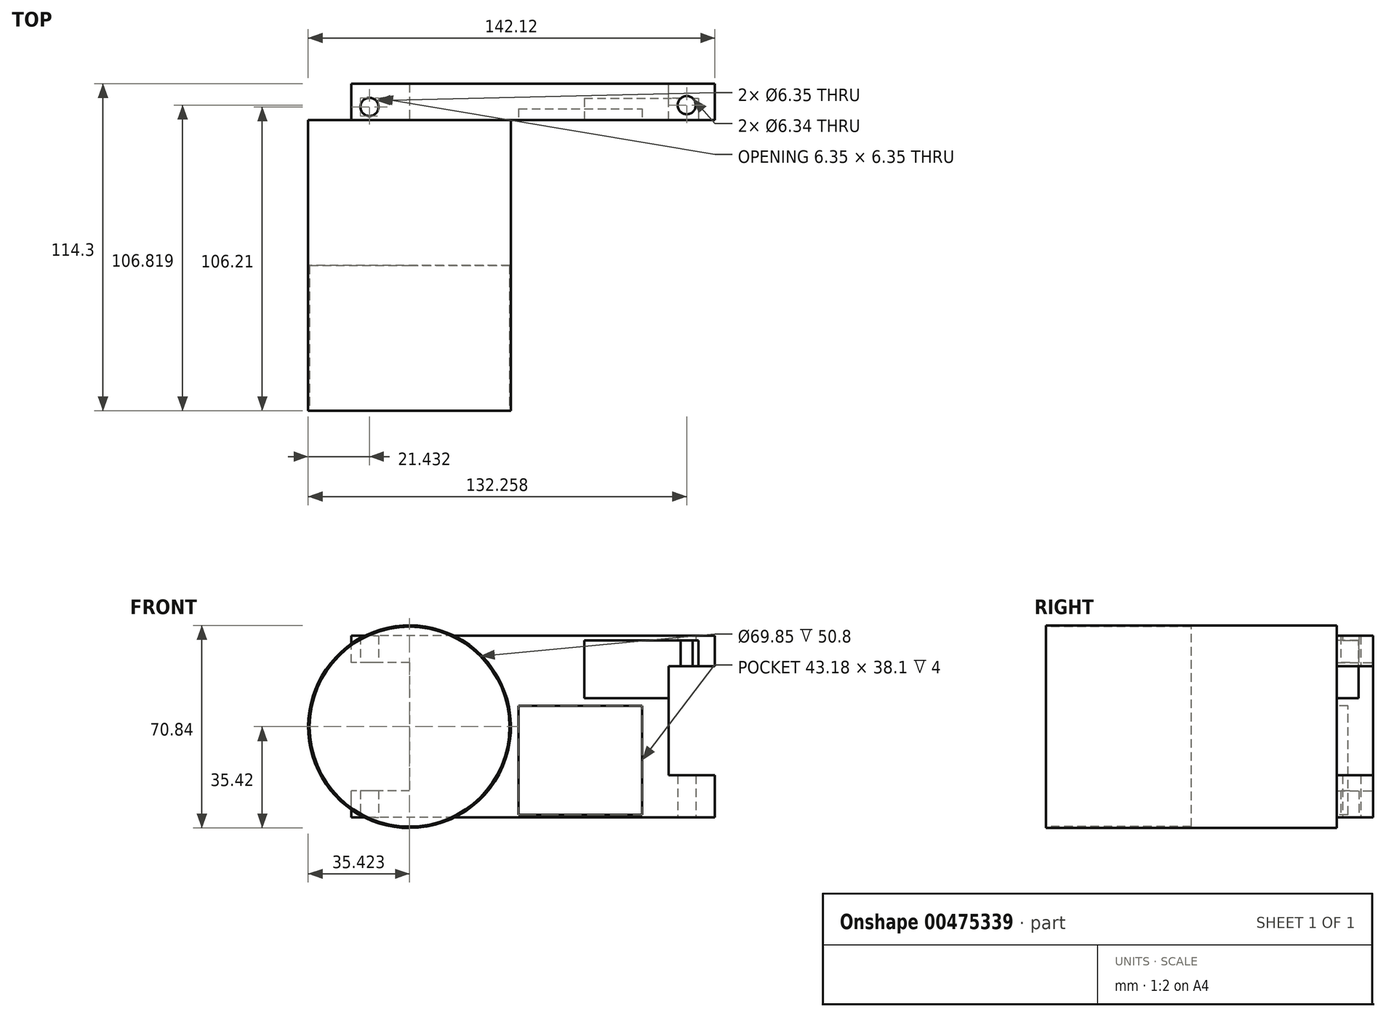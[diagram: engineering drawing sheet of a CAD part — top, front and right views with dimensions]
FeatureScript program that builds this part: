
annotation { "Feature Type Name" : "Feature", "Feature Type Description" : "" }
export const myFeature = defineFeature(function(context is Context, id is Id, definition is map)
    precondition{}
    {
        {
            var Q0;
            Q0=qCreatedBy(makeId("Front.planeOp"),FACE);
            var sketch = newSketch(context, id + "F0", { "sketchPlane" : qUnion([Q0])});
            skLineSegment(sketch, "E0.bottom", {"start": v(63.5, -31.75) * mm, "end": v(-63.5, -31.75) * mm});
            skLineSegment(sketch, "E0.top", {"start": v(63.5, 31.75) * mm, "end": v(-63.5, 31.75) * mm});
            skLineSegment(sketch, "E0.left", {"start": v(63.5, -31.75) * mm, "end": v(63.5, 31.75) * mm});
            skLineSegment(sketch, "E0.right", {"start": v(-63.5, -31.75) * mm, "end": v(-63.5, 31.75) * mm});
            skPoint(sketch, "E0.middle", {"position": v(0, 0) * mm});
            skSolve(sketch);
        }
        {
            var Q0;
            Q0 = qSketchRegion(id + "F0", true);
            extrude(context, id + "F1", {"entities" : qUnion([Q0]), "depth" : 12.7 * mm});
        }
        {
            var Q0;
            Q0=makeQuery(id+"F1.opExtrude","CAP_FACE",FACE,{"disambiguationData":[OSD([sQuery(id+"F0.wireOp",EDGE,"E0.bottom"),sQuery(id+"F0.wireOp",EDGE,"E0.top"),sQuery(id+"F0.wireOp",EDGE,"E0.left"),sQuery(id+"F0.wireOp",EDGE,"E0.right")])],"isStart":false});
            var sketch = newSketch(context, id + "F2", { "sketchPlane" : qUnion([Q0])});
            skLineSegment(sketch, "E1.bottom", {"start": v(-5.08, -30.75) * mm, "end": v(38.1, -30.75) * mm});
            skLineSegment(sketch, "E1.top", {"start": v(-5.08, 7.35) * mm, "end": v(38.1, 7.35) * mm});
            skLineSegment(sketch, "E1.left", {"start": v(-5.08, -30.75) * mm, "end": v(-5.08, 7.35) * mm});
            skLineSegment(sketch, "E1.right", {"start": v(38.1, -30.75) * mm, "end": v(38.1, 7.35) * mm});
            skPoint(sketch, "E1.middle", {"position": v(16.5, -11.7) * mm});
            skSolve(sketch);
        }
        {
            var Q0;
            Q0 = qSketchRegion(id + "F2", true);
            extrude(context, id + "F3", {"entities" : qUnion([Q0]), "operationType" : NewBodyOperationType.REMOVE, "oppositeDirection" : true, "depth" : 4 * mm});
        }
        {
            var Q0;
            Q0=makeQuery(id+"F1.opExtrude","CAP_FACE",FACE,{"disambiguationData":[OSD([sQuery(id+"F0.wireOp",EDGE,"E0.bottom"),sQuery(id+"F0.wireOp",EDGE,"E0.top"),sQuery(id+"F0.wireOp",EDGE,"E0.left"),sQuery(id+"F0.wireOp",EDGE,"E0.right")])],"isStart":false});
            var sketch = newSketch(context, id + "F4", { "sketchPlane" : qUnion([Q0])});
            skLineSegment(sketch, "E2.bottom", {"start": v(17.8, 9.95) * mm, "end": v(57.8, 9.95) * mm});
            skLineSegment(sketch, "E2.top", {"start": v(17.8, 30.1) * mm, "end": v(57.8, 30.1) * mm});
            skLineSegment(sketch, "E2.left", {"start": v(17.8, 9.95) * mm, "end": v(17.8, 30.1) * mm});
            skLineSegment(sketch, "E2.right", {"start": v(57.8, 9.95) * mm, "end": v(57.8, 30.1) * mm});
            skPoint(sketch, "E2.middle", {"position": v(37.8, 20.03) * mm});
            skSolve(sketch);
        }
        {
            var Q0;
            Q0 = qSketchRegion(id + "F4", true);
            extrude(context, id + "F5", {"entities" : qUnion([Q0]), "operationType" : NewBodyOperationType.REMOVE, "oppositeDirection" : true, "depth" : 7.62 * mm});
        }
        {
            var Q0;
            Q0=makeQuery(id+"F1.opExtrude","SWEPT_FACE",FACE,{"disambiguationData":[OSD([sQuery(id+"F0.wireOp",EDGE,"E0.bottom")])]});
            var sketch = newSketch(context, id + "F6", { "sketchPlane" : qUnion([Q0])});
            skCircle(sketch, "E3", {"center": v(53.64, 7.48) * mm, "radius": 3.17 * mm});
            skSolve(sketch);
        }
        {
            var Q0;
            Q0 = qSketchRegion(id + "F6", true);
            extrude(context, id + "F7", {"entities" : qUnion([Q0]), "operationType" : NewBodyOperationType.REMOVE, "endBound" : BoundingType.THROUGH_ALL, "oppositeDirection" : true, "depth" : 25.4 * mm});
        }
        {
            var Q0;
            Q0=makeQuery(id+"F1.opExtrude","SWEPT_FACE",FACE,{"disambiguationData":[OSD([sQuery(id+"F0.wireOp",EDGE,"E0.bottom")])]});
            var sketch = newSketch(context, id + "F8", { "sketchPlane" : qUnion([Q0])});
            skCircle(sketch, "E4", {"center": v(-57.19, 8.1) * mm, "radius": 3.18 * mm});
            skSolve(sketch);
        }
        {
            var Q0;
            Q0 = qSketchRegion(id + "F8", true);
            extrude(context, id + "F9", {"entities" : qUnion([Q0]), "operationType" : NewBodyOperationType.REMOVE, "endBound" : BoundingType.THROUGH_ALL, "oppositeDirection" : true, "depth" : 25.4 * mm});
        }
        {
            var Q0;
            Q0=makeQuery(id+"F1.opExtrude","CAP_FACE",FACE,{"disambiguationData":[OSD([sQuery(id+"F0.wireOp",EDGE,"E0.bottom"),sQuery(id+"F0.wireOp",EDGE,"E0.top"),sQuery(id+"F0.wireOp",EDGE,"E0.left"),sQuery(id+"F0.wireOp",EDGE,"E0.right")])],"isStart":true});
            var sketch = newSketch(context, id + "F10", { "sketchPlane" : qUnion([Q0])});
            skLineSegment(sketch, "E5.bottom", {"start": v(-47.3, -17) * mm, "end": v(-79.7, -17) * mm});
            skLineSegment(sketch, "E5.top", {"start": v(-47.3, 21.15) * mm, "end": v(-79.7, 21.15) * mm});
            skLineSegment(sketch, "E5.left", {"start": v(-47.3, -17) * mm, "end": v(-47.3, 21.15) * mm});
            skLineSegment(sketch, "E5.right", {"start": v(-79.7, -17) * mm, "end": v(-79.7, 21.15) * mm});
            skPoint(sketch, "E5.middle", {"position": v(-63.5, 2.07) * mm});
            skSolve(sketch);
        }
        {
            var Q0;
            Q0 = qSketchRegion(id + "F10", true);
            extrude(context, id + "F11", {"entities" : qUnion([Q0]), "operationType" : NewBodyOperationType.REMOVE, "endBound" : BoundingType.THROUGH_ALL, "oppositeDirection" : true, "depth" : 25.4 * mm});
        }
        {
            var Q0;
            Q0=makeQuery(id+"F1.opExtrude","CAP_FACE",FACE,{"disambiguationData":[OSD([sQuery(id+"F0.wireOp",EDGE,"E0.bottom"),sQuery(id+"F0.wireOp",EDGE,"E0.top"),sQuery(id+"F0.wireOp",EDGE,"E0.left"),sQuery(id+"F0.wireOp",EDGE,"E0.right")])],"isStart":false});
            var sketch = newSketch(context, id + "F12", { "sketchPlane" : qUnion([Q0])});
            skLineSegment(sketch, "E6.bottom", {"start": v(-43.2, 22.38) * mm, "end": v(-83.8, 22.38) * mm});
            skLineSegment(sketch, "E6.top", {"start": v(-43.2, -22.38) * mm, "end": v(-83.8, -22.38) * mm});
            skLineSegment(sketch, "E6.left", {"start": v(-43.2, 22.38) * mm, "end": v(-43.2, -22.38) * mm});
            skLineSegment(sketch, "E6.right", {"start": v(-83.8, 22.38) * mm, "end": v(-83.8, -22.38) * mm});
            skPoint(sketch, "E6.middle", {"position": v(-63.5, 0) * mm});
            skSolve(sketch);
        }
        {
            var Q0;
            Q0 = qSketchRegion(id + "F12", true);
            extrude(context, id + "F13", {"entities" : qUnion([Q0]), "operationType" : NewBodyOperationType.REMOVE, "endBound" : BoundingType.THROUGH_ALL, "oppositeDirection" : true, "depth" : 25.4 * mm});
        }
        {
            var Q0;
            Q0=makeQuery(id+"F1.opExtrude","CAP_FACE",FACE,{"disambiguationData":[OSD([sQuery(id+"F0.wireOp",EDGE,"E0.bottom"),sQuery(id+"F0.wireOp",EDGE,"E0.top"),sQuery(id+"F0.wireOp",EDGE,"E0.left"),sQuery(id+"F0.wireOp",EDGE,"E0.right")])],"isStart":false});
            var sketch = newSketch(context, id + "F14", { "sketchPlane" : qUnion([Q0])});
            skCircle(sketch, "E7", {"center": v(-43.2, 0) * mm, "radius": 35.42 * mm});
            skSolve(sketch);
        }
        {
            var Q0;
            Q0 = qSketchRegion(id + "F14", true);
            extrude(context, id + "F15", {"entities" : qUnion([Q0]), "operationType" : NewBodyOperationType.ADD, "depth" : 101.6 * mm});
        }
        {
            var Q0;
            Q0=makeQuery(id+"F15.opExtrude","CAP_FACE",FACE,{"disambiguationData":[OSD([sQuery(id+"F14.wireOp",EDGE,"E7")])],"isStart":false});
            var sketch = newSketch(context, id + "F16", { "sketchPlane" : qUnion([Q0])});
            skCircle(sketch, "E8", {"center": v(-43.2, 0) * mm, "radius": 34.93 * mm});
            skSolve(sketch);
        }
        {
            var Q0;
            Q0 = qSketchRegion(id + "F16", true);
            extrude(context, id + "F17", {"entities" : qUnion([Q0]), "operationType" : NewBodyOperationType.REMOVE, "oppositeDirection" : true, "depth" : 50.8 * mm});
        }
    });
